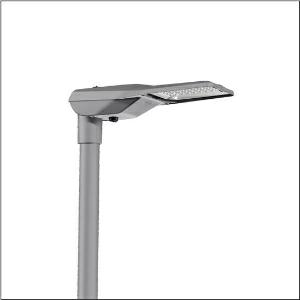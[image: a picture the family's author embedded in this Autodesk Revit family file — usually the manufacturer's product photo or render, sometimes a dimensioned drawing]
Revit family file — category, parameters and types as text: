
# Revit family: streetlight_sl_21_iq_mini___st0_5a_5xe2b31y08hb_0ff0
name_source: partatom
category: Lighting Fixtures
units: mm (PartAtom-declared; Revit-internal decimal feet)

## family parameters
Cut with Voids When Loaded = No
Host = Face
Light Source = No
Part Type = Normal
Room Calculation Point = No
Round Connector Dimension = Use Diameter
Shared = No

## types (1)
- --- (1 x LED, 9750 lm, 71 W, 3000K)
    Apparent Load = 71 VA
    CIE Flux Codes = 41 75 97 100 100
    Color Rendering = 70
    Color Temperature = 3000K
    Default Elevation = 1800 mm
    Description = Streetlight SL 21 iQ mini, mast luminaire, primary light control with lens, of PMMA, primary optical cover: cover, of toughened safety glass, transparent, light distribution: ST0.5a, light emission: direct distribution, primary light characteristic: asymmetric, installation type: post-top, side-entry, LED, High Power LED, rated luminous flux: 9.750lm, luminous efficacy: 137lm/W, light colour: 730, colour temperature: 3000K, control: presetting dimming logarithmic, Street-Remote, Auto-Match, Temp-Guard, Lumen-Switch, Night-Set, Smart-Wire, Light-Fading, Desk-Remote (wireless, voltage-free reading and setting of iQ features in the workshop via application-optimized NFC function/RFID function), optimised constant luminous flux control (CLO 2.0), mains connection: 220..240V, AC, 50/60Hz, start of lifetime: 71W, end of service life: 75W, reduction: 30W, luminaire housing, of diecast aluminium, powder-coated, Siteco® metallic grey (DB 702S), corrosivity category C5 mid according to DIN EN ISO 12944, please order mast flange separately, inclination adjustable: 0°, 5°, 10°, 15°, sealing non-destructively replaceable, multi-level sealing system, length: 628mm, width: 235mm, height: 110mm, mast flange for spigot size: 42mm (side-entry): 5XC10008XM4, 60/48mm (side-entry/post-top): 5XC10108XM2, 76/60mm (side-entry/post-top): 5XC10108XM1, Smart Interface below and above, protection rating (complete): IP66, insulation class (complete): insulation class II (safety insulation), certification: CE, ENEC, ENEC+, VDE, impact resistance: IK09, permissible operating ambient temperature for outdoor applications: -40..+50°C, standard-compliant lighting for roads and squares, packaging unit: 1 piece

Light Distribution: ST0.5a
    Height = 110 mm
    Lamp = 1 x LED
    Lamp Light Flux = 9750 lm
    Lamp Power = 71 W
    Lamp count = 1
    Length = 625 mm
    Luminous efficacy = 137 lm/W
    Manufacturer = Siteco
    ModVariant = No
    Model = 5XE2B31Y08HB
    Number of Poles = 1
    OnlyDefault = Yes
    Power Factor = 1
    Product Name = Streetlight SL 21 iQ mini | ST0.5a
    Product group = mast luminaire | pylon top
    ProductGroupID = 6100
    Protection Class = Protection class II
    Protection Degree = IP 66
    RLX_Detail_Level = 1
    RLX_Emergency_Light_Flux = 0 lm
    RLX_Emergency_Type = 0
    RLX_Emergency_Type_DB = No
    RlxData = <blob elided: 103637 chars, md5=24ff5c99>
    Socket = socket
    Standby Power = 0 W
    System Light Flux = 9750 lm
    System Power = 71 W
    Type Comments = factory setting: luminous flux: 100 % | dim-lin: 254 | 716 mA
    Type Image = l_1003514.jpg
    URL = http://relux.com
    VarID = @adj_046143
    Voltage = 0 V
    Weight = 0.00 kg
    Width = 234 mm

## geometry (parser evidence)
native form markers: Blend x4, Sweep x10
no freeform markers — native parametric forms only
